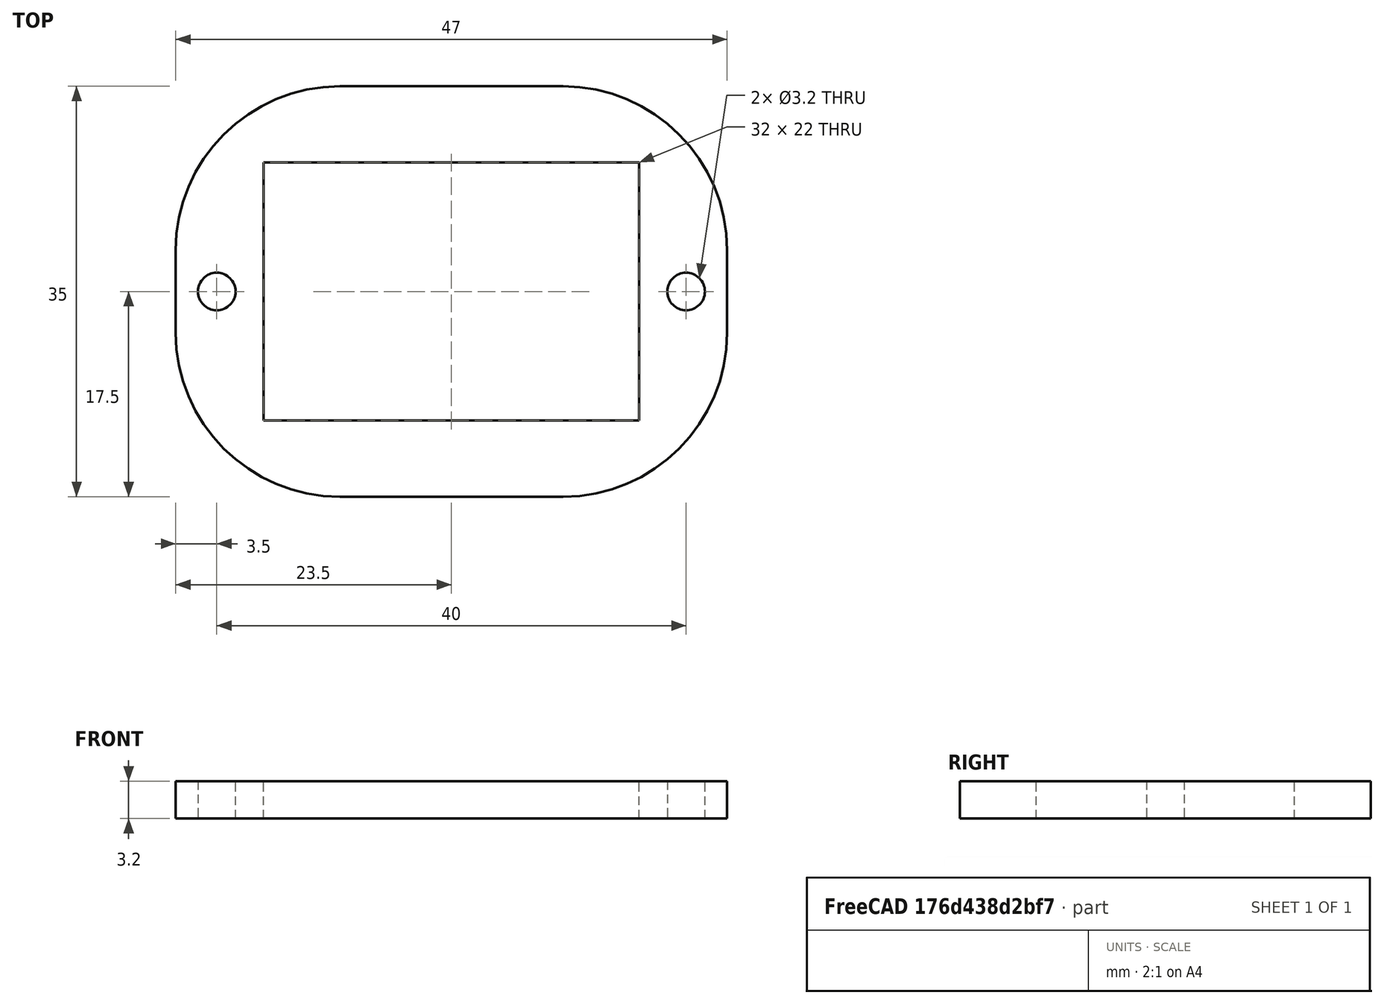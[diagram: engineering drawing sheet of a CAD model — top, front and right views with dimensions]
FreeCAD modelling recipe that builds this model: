
FCSTD DOCUMENT  (FreeCAD 0.21R33668 +26 (Git))
Label: 0_Base_Switch
License: All rights reserved
LicenseURL: https://en.wikipedia.org/wiki/All_rights_reserved
objects: Sketcher::SketchObject×1, PartDesign::Pad×1, PartDesign::Body×1
note: 4 computed .brp shape members not serialized (recipe doc carries the construction recipe); baked Part::Feature solids carry a one-line shape summary decoded from their .brp

FEATURE [Sketcher::SketchObject] Sketch
  FullyConstrained = true
  MapMode = 5
  Support = -> [XY_Plane]
  sketch-geometry (14):
    g0: LineSegment StartX=-9.5 StartY=17.5 StartZ=0 EndX=9.5 EndY=17.5 EndZ=0
    g1: LineSegment StartX=23.5 StartY=3.5 StartZ=0 EndX=23.5 EndY=-3.5 EndZ=0
    g2: LineSegment StartX=9.5 StartY=-17.5 StartZ=0 EndX=-9.5 EndY=-17.5 EndZ=0
    g3: LineSegment StartX=-23.5 StartY=-3.5 StartZ=0 EndX=-23.5 EndY=3.5 EndZ=0
    g4: LineSegment StartX=-16 StartY=11 StartZ=0 EndX=16 EndY=11 EndZ=0
    g5: LineSegment StartX=16 StartY=11 StartZ=0 EndX=16 EndY=-11 EndZ=0
    g6: LineSegment StartX=16 StartY=-11 StartZ=0 EndX=-16 EndY=-11 EndZ=0
    g7: LineSegment StartX=-16 StartY=-11 StartZ=0 EndX=-16 EndY=11 EndZ=0
    g8: Circle CenterX=-20 CenterY=0 CenterZ=0 NormalX=0 NormalY=0 NormalZ=1 AngleXU=0 Radius=1.6
    g9: Circle CenterX=20 CenterY=0 CenterZ=0 NormalX=0 NormalY=0 NormalZ=1 AngleXU=0 Radius=1.6
    g10: ArcOfCircle CenterX=-9.5 CenterY=3.5 CenterZ=0 NormalX=0 NormalY=0 NormalZ=1 AngleXU=0 Radius=14 StartAngle=1.5708 EndAngle=3.14159
    g11: ArcOfCircle CenterX=9.5 CenterY=3.5 CenterZ=0 NormalX=0 NormalY=0 NormalZ=1 AngleXU=0 Radius=14 StartAngle=0 EndAngle=1.5708
    g12: ArcOfCircle CenterX=9.5 CenterY=-3.5 CenterZ=0 NormalX=0 NormalY=0 NormalZ=1 AngleXU=0 Radius=14 StartAngle=4.71239 EndAngle=6.28319
    g13: ArcOfCircle CenterX=-9.5 CenterY=-3.5 CenterZ=0 NormalX=0 NormalY=0 NormalZ=1 AngleXU=0 Radius=14 StartAngle=3.14159 EndAngle=4.71239
  constraints (34):
    c: Coincident(g4,g5)
    c: Coincident(g5,g6)
    c: Coincident(g6,g7)
    c: Coincident(g7,g4)
    c: Horizontal(g6)
    c: Vertical(g5)
    c: PointOnObject(g9,g-1)
    c: Equal(g9,g8)
    c: Symmetric(g4,g6,g-1)
    c: Symmetric(g4,g4,g-2)
    c: Vertical(g1)
    c: Horizontal(g2)
    c: Symmetric(g9,g8,g-2)
    c: DistanceX(g4,g4) = 32
    c: DistanceY(g7,g7) = 22
    c: Diameter(g9) = 3.2
    c: DistanceX(g5,g9) = 4
    c: Tangent(g0,g10) = 1.5708
    c: Tangent(g3,g10) = 1.5708
    c: Tangent(g0,g11) = 1.5708
    c: Tangent(g1,g11) = 1.5708
    c: Tangent(g1,g12) = 1.5708
    c: Tangent(g2,g12) = 1.5708
    c: Tangent(g2,g13) = 1.5708
    c: Tangent(g3,g13) = 1.5708
    c: Equal(g10,g11)
    c: Equal(g11,g12)
    c: Equal(g12,g13)
    c: Radius(g10) = 14
    c: DistanceY(g2,g0) = 35
    c: Symmetric(g2,g0,g-1)
    c: Horizontal(g0)
    c: Vertical(g3)
    c: DistanceX(g3,g1) = 47
FEATURE [PartDesign::Pad] Pad
  Direction = (0,0,1)
  Length = 3.2
  Length2 = 10
  Profile = -> Sketch
  ReferenceAxis = -> Sketch [N_Axis]
  Type = 0
FEATURE [PartDesign::Body] Body
  Group = -> [Sketch,Pad]
  Origin = -> Origin
  Tip = -> Pad
